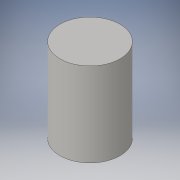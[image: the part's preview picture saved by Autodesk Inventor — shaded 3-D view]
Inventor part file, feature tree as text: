
AUTODESK INVENTOR PART (.ipt)
format: ipt  version: 2016 (Build 200138000, 138)  size: 83,968 bytes
history: native  units: in
note: dims shown in document units (in); Inventor stores cm internally (conversion verified against a paired STEP export)
features: sketch x2, extrude x1
ambient origin geometry x8: Origin, YZ Plane, XZ Plane, XY Plane, X Axis, Y Axis, Z Axis, Center Point
bodies: Solid1 (feature_tree)
feature tree (3):
  sketch  "Sketch1"  dims[d0=0.3937in d1=0.5512in d2=0.0in]
  extrude  "Extrusion1"  Depth=0.5512in TaperAngle=0.0deg
  sketch  "Sketch2"
